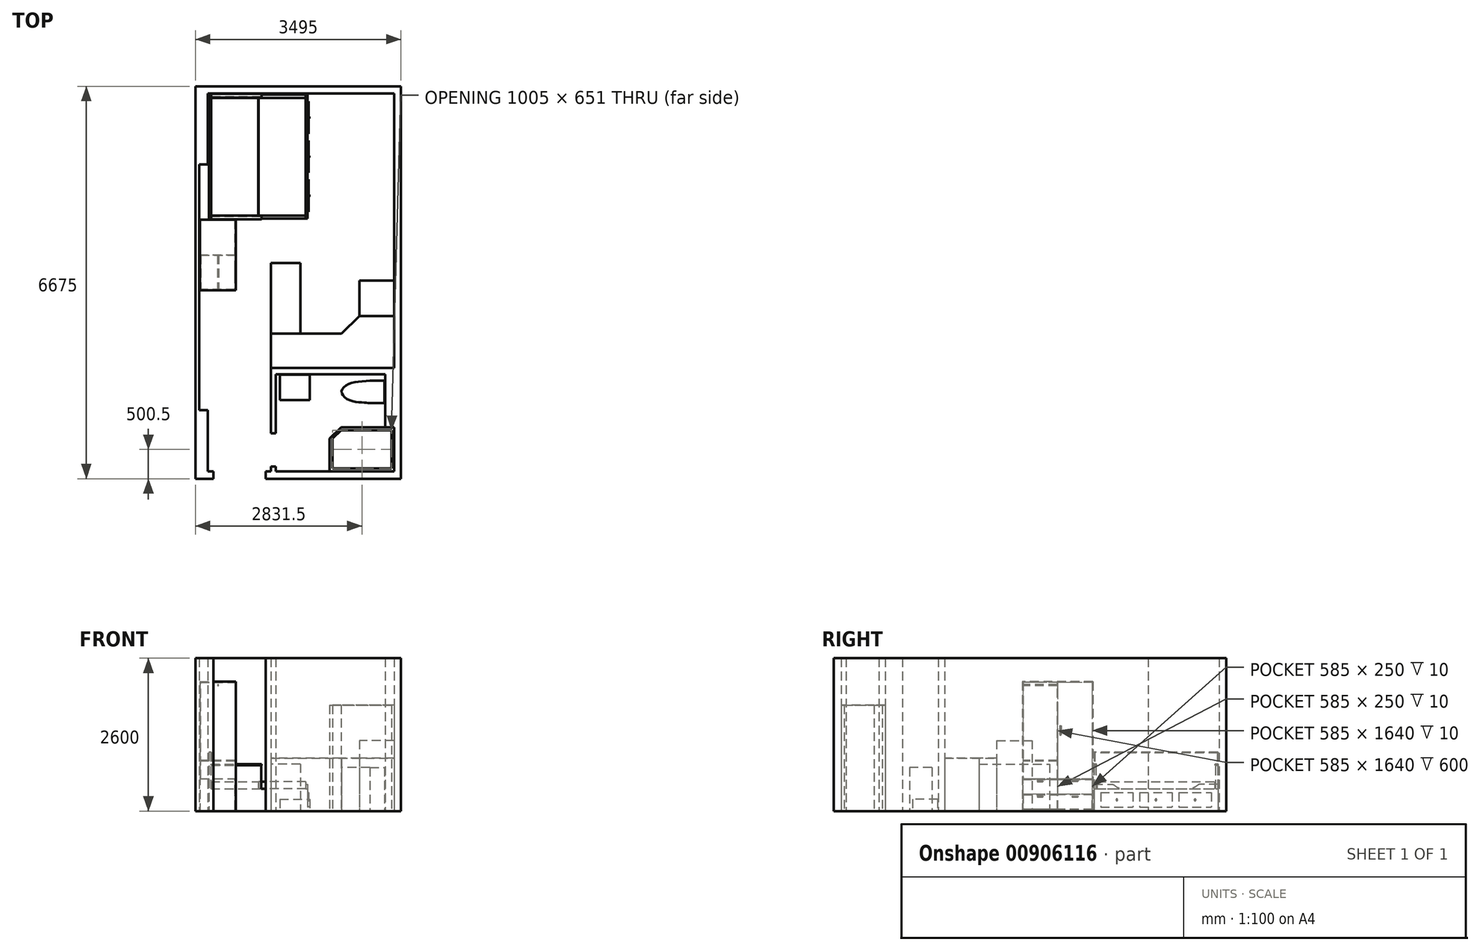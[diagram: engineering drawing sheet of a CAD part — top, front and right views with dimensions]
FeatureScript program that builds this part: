
annotation { "Feature Type Name" : "Feature", "Feature Type Description" : "" }
export const myFeature = defineFeature(function(context is Context, id is Id, definition is map)
    precondition{}
    {
        {
            var Q0;
            Q0=qCreatedBy(makeId("Top.planeOp"),FACE);
            var sketch = newSketch(context, id + "F0", { "sketchPlane" : qUnion([Q0])});
            skLineSegment(sketch, "E0", {"start": v(0, 0) * mm, "end": v(-2302, 0) * mm});
            skLineSegment(sketch, "E1", {"start": v(-3191, 0) * mm, "end": v(-3495, 0) * mm});
            skLineSegment(sketch, "E2", {"start": v(0, 0) * mm, "end": v(0, 6675) * mm});
            skLineSegment(sketch, "E3", {"start": v(0, 6675) * mm, "end": v(-3495, 6675) * mm});
            skLineSegment(sketch, "E4", {"start": v(-3495, 6675) * mm, "end": v(-3495, 0) * mm});
            skLineSegment(sketch, "E5", {"start": v(-2302, 0) * mm, "end": v(-2302, 125) * mm});
            skLineSegment(sketch, "E6", {"start": v(-2302, 125) * mm, "end": v(-2211, 125) * mm});
            skLineSegment(sketch, "E7", {"start": v(-2211, 125) * mm, "end": v(-2211, 211) * mm});
            skLineSegment(sketch, "E8", {"start": v(-2211, 211) * mm, "end": v(-2129, 211) * mm});
            skLineSegment(sketch, "E9", {"start": v(-2129, 211) * mm, "end": v(-2129, 125) * mm});
            skLineSegment(sketch, "E10", {"start": v(-2129, 125) * mm, "end": v(-116, 125) * mm});
            skLineSegment(sketch, "E11", {"start": v(-116, 125) * mm, "end": v(-116, 876) * mm});
            skLineSegment(sketch, "E12", {"start": v(-116, 876) * mm, "end": v(-269, 876) * mm});
            skLineSegment(sketch, "E13", {"start": v(-269, 876) * mm, "end": v(-269, 1780) * mm});
            skLineSegment(sketch, "E14", {"start": v(0, 1780) * mm, "end": v(-2129, 1780) * mm});
            skLineSegment(sketch, "E15", {"start": v(-2129, 1780) * mm, "end": v(-2129, 771.47) * mm});
            skLineSegment(sketch, "E16", {"start": v(-2129, 771.47) * mm, "end": v(-2211, 771.47) * mm});
            skLineSegment(sketch, "E17", {"start": v(-2211, 771.47) * mm, "end": v(-2211, 1887) * mm});
            skLineSegment(sketch, "E18", {"start": v(-2211, 1887) * mm, "end": v(0, 1887) * mm});
            skLineSegment(sketch, "E19", {"start": v(-116, 1887) * mm, "end": v(-116, 6555) * mm});
            skLineSegment(sketch, "E20", {"start": v(-116, 6555) * mm, "end": v(-3285, 6555) * mm});
            skLineSegment(sketch, "E21", {"start": v(-3285, 6555) * mm, "end": v(-3285, 5348) * mm});
            skLineSegment(sketch, "E22", {"start": v(-3285, 5348) * mm, "end": v(-3430, 5348) * mm});
            skLineSegment(sketch, "E23", {"start": v(-3430, 5348) * mm, "end": v(-3430, 1167) * mm});
            skLineSegment(sketch, "E24", {"start": v(-3495, 0) * mm, "end": v(-3191, 0) * mm});
            skLineSegment(sketch, "E25", {"start": v(-3430, 1167) * mm, "end": v(-3285, 1167) * mm});
            skLineSegment(sketch, "E26", {"start": v(-3191, 0) * mm, "end": v(-3191, 125) * mm});
            skLineSegment(sketch, "E27", {"start": v(-3191, 125) * mm, "end": v(-3285, 125) * mm});
            skLineSegment(sketch, "E28", {"start": v(-3285, 125) * mm, "end": v(-3285, 1167) * mm});
            skSolve(sketch);
        }
        {
            var Q0;
            {var subQ0=sQuery(id+"F0.wireOp",EDGE,"E0");Q0=makeQuery(id+"F0.imprint","IMPRINT",FACE,{"disambiguationData":[TD([[makeQuery(id+"F0.imprint","IMPRINT",EDGE,{"derivedFrom":subQ0}),-1.0]])]});}
            var Q1;
            {var subQ1=sQuery(id+"F0.wireOp",EDGE,"E3");Q1=makeQuery(id+"F0.imprint","IMPRINT",FACE,{"disambiguationData":[TD([[makeQuery(id+"F0.imprint","IMPRINT",EDGE,{"derivedFrom":subQ1}),1.0]])]});}
            var Q2;
            {var subQ2=sQuery(id+"F0.wireOp",EDGE,"E15");Q2=makeQuery(id+"F0.imprint","IMPRINT",FACE,{"disambiguationData":[TD([[makeQuery(id+"F0.imprint","IMPRINT",EDGE,{"derivedFrom":subQ2}),-1.0]])]});}
            extrude(context, id + "F1", {"entities" : qUnion([Q0, Q1, Q2]), "depth" : 2600 * mm, "offsetDistance" : 25 * mm});
        }
        {
            var Q0;
            Q0=makeQuery(id+"F1.opExtrude","CAP_FACE",FACE,{"disambiguationData":[OSD([sQuery(id+"F0.wireOp",EDGE,"E0"),sQuery(id+"F0.wireOp",EDGE,"E2"),sQuery(id+"F0.wireOp",EDGE,"E3"),sQuery(id+"F0.wireOp",EDGE,"E4"),sQuery(id+"F0.wireOp",EDGE,"E5"),sQuery(id+"F0.wireOp",EDGE,"E6"),sQuery(id+"F0.wireOp",EDGE,"E7"),sQuery(id+"F0.wireOp",EDGE,"E8"),sQuery(id+"F0.wireOp",EDGE,"E9"),sQuery(id+"F0.wireOp",EDGE,"E10"),sQuery(id+"F0.wireOp",EDGE,"E11"),sQuery(id+"F0.wireOp",EDGE,"E12"),sQuery(id+"F0.wireOp",EDGE,"E13"),sQuery(id+"F0.wireOp",EDGE,"E14"),sQuery(id+"F0.wireOp",EDGE,"E15"),sQuery(id+"F0.wireOp",EDGE,"E16"),sQuery(id+"F0.wireOp",EDGE,"E17"),sQuery(id+"F0.wireOp",EDGE,"E18"),sQuery(id+"F0.wireOp",EDGE,"E19"),sQuery(id+"F0.wireOp",EDGE,"E20"),sQuery(id+"F0.wireOp",EDGE,"E21"),sQuery(id+"F0.wireOp",EDGE,"E22"),sQuery(id+"F0.wireOp",EDGE,"E23"),sQuery(id+"F0.wireOp",EDGE,"E24"),sQuery(id+"F0.wireOp",EDGE,"E25"),sQuery(id+"F0.wireOp",EDGE,"E26"),sQuery(id+"F0.wireOp",EDGE,"E27"),sQuery(id+"F0.wireOp",EDGE,"E28")])],"isStart":true});
            var sketch = newSketch(context, id + "F2", { "sketchPlane" : qUnion([Q0])});
            skLineSegment(sketch, "E29", {"start": v(0, 0) * mm, "end": v(0, -2770) * mm, "construction": true});
            skLineSegment(sketch, "E30", {"start": v(-116, -1887) * mm, "end": v(-116, -2770) * mm});
            skLineSegment(sketch, "E31", {"start": v(-116, -2770) * mm, "end": v(-705, -2770) * mm});
            skLineSegment(sketch, "E32", {"start": v(-705, -2770) * mm, "end": v(-1011, -2468) * mm});
            skLineSegment(sketch, "E33", {"start": v(-1011, -2468) * mm, "end": v(-1011, -1887) * mm});
            skLineSegment(sketch, "E34", {"start": v(-1011, -1887) * mm, "end": v(-116, -1887) * mm});
            skLineSegment(sketch, "E35", {"start": v(-1011, -2468) * mm, "end": v(-2211, -2468) * mm});
            skLineSegment(sketch, "E36", {"start": v(-2211, -2468) * mm, "end": v(-2211, -1887) * mm});
            skLineSegment(sketch, "E37", {"start": v(-2211, -1887) * mm, "end": v(-1011, -1887) * mm});
            skSolve(sketch);
        }
        {
            var Q0;
            Q0=makeQuery(id+"F2.imprint","IMPRINT",FACE,{"disambiguationData":[TD([[makeQuery(id+"F2.imprint","IMPRINT",EDGE,{"derivedFrom":sQuery(id+"F2.wireOp",EDGE,"E33")}),1.0]])]});
            var Q1;
            Q1=makeQuery(id+"F2.imprint","IMPRINT",FACE,{"disambiguationData":[TD([[makeQuery(id+"F2.imprint","IMPRINT",EDGE,{"derivedFrom":sQuery(id+"F2.wireOp",EDGE,"E30")}),-1.0]])]});
            extrude(context, id + "F3", {"entities" : qUnion([Q0, Q1]), "oppositeDirection" : true, "depth" : 900 * mm, "offsetDistance" : 25 * mm});
        }
        {
            var Q0;
            Q0=makeQuery(id+"F3.opExtrude","CAP_FACE",FACE,{"disambiguationData":[OSD([sQuery(id+"F2.wireOp",EDGE,"E30"),sQuery(id+"F2.wireOp",EDGE,"E31"),sQuery(id+"F2.wireOp",EDGE,"E32"),sQuery(id+"F2.wireOp",EDGE,"E34"),sQuery(id+"F2.wireOp",EDGE,"E35"),sQuery(id+"F2.wireOp",EDGE,"E36"),sQuery(id+"F2.wireOp",EDGE,"E37")])],"isStart":true});
            var sketch = newSketch(context, id + "F4", { "sketchPlane" : qUnion([Q0])});
            skLineSegment(sketch, "E38", {"start": v(-705, -2770) * mm, "end": v(-705, -3370) * mm});
            skLineSegment(sketch, "E39", {"start": v(-705, -3370) * mm, "end": v(-116, -3370) * mm});
            skLineSegment(sketch, "E40", {"start": v(-116, -3370) * mm, "end": v(-116, -2770) * mm});
            skLineSegment(sketch, "E41", {"start": v(-116, -2770) * mm, "end": v(-705, -2770) * mm});
            skSolve(sketch);
        }
        {
            var Q0;
            Q0=makeQuery(id+"F4.imprint","IMPRINT",FACE,{"disambiguationData":[TD([[makeQuery(id+"F4.imprint","IMPRINT",EDGE,{"derivedFrom":sQuery(id+"F4.wireOp",EDGE,"E38")}),1.0]])]});
            extrude(context, id + "F5", {"entities" : qUnion([Q0]), "oppositeDirection" : true, "depth" : 1200 * mm, "offsetDistance" : 25 * mm});
        }
        {
            var Q0;
            Q0=makeQuery(id+"F5.boolean.opBoolean","MERGE",FACE,{"derivedFrom":[makeQuery(id+"F3.opExtrude","CAP_FACE",FACE,{"disambiguationData":[OSD([sQuery(id+"F2.wireOp",EDGE,"E30"),sQuery(id+"F2.wireOp",EDGE,"E31"),sQuery(id+"F2.wireOp",EDGE,"E32"),sQuery(id+"F2.wireOp",EDGE,"E34"),sQuery(id+"F2.wireOp",EDGE,"E35"),sQuery(id+"F2.wireOp",EDGE,"E36"),sQuery(id+"F2.wireOp",EDGE,"E37")])],"isStart":true}),makeQuery(id+"F5.opExtrude","CAP_FACE",FACE,{"disambiguationData":[OSD([sQuery(id+"F4.wireOp",EDGE,"E38"),sQuery(id+"F4.wireOp",EDGE,"E39"),sQuery(id+"F4.wireOp",EDGE,"E40"),sQuery(id+"F4.wireOp",EDGE,"E41")])],"isStart":true})]});
            var sketch = newSketch(context, id + "F6", { "sketchPlane" : qUnion([Q0])});
            skLineSegment(sketch, "E42", {"start": v(-3268.16, -6533.7) * mm, "end": v(-3268.16, -4423.7) * mm});
            skLineSegment(sketch, "E43", {"start": v(-3268.16, -4423.7) * mm, "end": v(-1588.16, -4423.7) * mm});
            skLineSegment(sketch, "E44", {"start": v(-1588.16, -4423.7) * mm, "end": v(-1588.16, -6533.7) * mm});
            skLineSegment(sketch, "E45", {"start": v(-1588.16, -6533.7) * mm, "end": v(-3268.16, -6533.7) * mm});
            skSolve(sketch);
        }
        {
            var Q0;
            Q0=makeQuery(id+"F6.imprint","IMPRINT",FACE,{"disambiguationData":[TD([[makeQuery(id+"F6.imprint","IMPRINT",EDGE,{"derivedFrom":sQuery(id+"F6.wireOp",EDGE,"E42")}),-1.0]])]});
            extrude(context, id + "F7", {"entities" : qUnion([Q0]), "oppositeDirection" : true, "depth" : 800 * mm, "offsetDistance" : 25 * mm});
        }
        {
            var Q0;
            Q0=makeQuery(id+"F7.opExtrude","CAP_FACE",FACE,{"disambiguationData":[OSD([sQuery(id+"F6.wireOp",EDGE,"E42"),sQuery(id+"F6.wireOp",EDGE,"E43"),sQuery(id+"F6.wireOp",EDGE,"E44"),sQuery(id+"F6.wireOp",EDGE,"E45")])],"isStart":true});
            var sketch = newSketch(context, id + "F8", { "sketchPlane" : qUnion([Q0])});
            skLineSegment(sketch, "E46.bottom", {"start": v(-3418.16, -4406.84) * mm, "end": v(-2808.16, -4406.84) * mm});
            skLineSegment(sketch, "E46.top", {"start": v(-3418.16, -3206.84) * mm, "end": v(-2808.16, -3206.84) * mm});
            skLineSegment(sketch, "E46.left", {"start": v(-3418.16, -4406.84) * mm, "end": v(-3418.16, -3206.84) * mm});
            skLineSegment(sketch, "E46.right", {"start": v(-2808.16, -4406.84) * mm, "end": v(-2808.16, -3206.84) * mm});
            skSolve(sketch);
        }
        {
            var Q0;
            Q0=makeQuery(id+"F8.imprint","IMPRINT",FACE,{"disambiguationData":[TD([[makeQuery(id+"F8.imprint","IMPRINT",EDGE,{"derivedFrom":sQuery(id+"F8.wireOp",EDGE,"E46.bottom")}),1.0]])]});
            extrude(context, id + "F9", {"entities" : qUnion([Q0]), "oppositeDirection" : true, "depth" : 2200 * mm, "offsetDistance" : 25 * mm});
        }
        {
            var Q0;
            Q0=makeQuery(id+"F3.opExtrude","CAP_FACE",FACE,{"disambiguationData":[OSD([sQuery(id+"F2.wireOp",EDGE,"E30"),sQuery(id+"F2.wireOp",EDGE,"E31"),sQuery(id+"F2.wireOp",EDGE,"E32"),sQuery(id+"F2.wireOp",EDGE,"E34"),sQuery(id+"F2.wireOp",EDGE,"E35"),sQuery(id+"F2.wireOp",EDGE,"E36"),sQuery(id+"F2.wireOp",EDGE,"E37")])],"isStart":true});
            var sketch = newSketch(context, id + "F10", { "sketchPlane" : qUnion([Q0])});
            skLineSegment(sketch, "E47", {"start": v(-2211, -2468) * mm, "end": v(-2211, -3668) * mm});
            skLineSegment(sketch, "E48", {"start": v(-2211, -3668) * mm, "end": v(-1711, -3668) * mm});
            skLineSegment(sketch, "E49", {"start": v(-1711, -3668) * mm, "end": v(-1711, -2468) * mm});
            skLineSegment(sketch, "E50", {"start": v(-1711, -2468) * mm, "end": v(-2211, -2468) * mm});
            skSolve(sketch);
        }
        {
            var Q0;
            Q0=makeQuery(id+"F10.imprint","IMPRINT",FACE,{"disambiguationData":[TD([[makeQuery(id+"F10.imprint","IMPRINT",EDGE,{"derivedFrom":sQuery(id+"F10.wireOp",EDGE,"E47")}),1.0]])]});
            extrude(context, id + "F11", {"entities" : qUnion([Q0]), "oppositeDirection" : true, "depth" : 800 * mm, "offsetDistance" : 25 * mm});
        }
        {
            var Q0;
            Q0=makeQuery(id+"F3.opExtrude","CAP_FACE",FACE,{"disambiguationData":[OSD([sQuery(id+"F2.wireOp",EDGE,"E30"),sQuery(id+"F2.wireOp",EDGE,"E31"),sQuery(id+"F2.wireOp",EDGE,"E32"),sQuery(id+"F2.wireOp",EDGE,"E34"),sQuery(id+"F2.wireOp",EDGE,"E35"),sQuery(id+"F2.wireOp",EDGE,"E36"),sQuery(id+"F2.wireOp",EDGE,"E37")])],"isStart":true});
            var sketch = newSketch(context, id + "F12", { "sketchPlane" : qUnion([Q0])});
            skLineSegment(sketch, "E51.bottom", {"start": v(-2061, -1768.17) * mm, "end": v(-1551, -1768.17) * mm});
            skLineSegment(sketch, "E51.top", {"start": v(-2061, -1338.17) * mm, "end": v(-1551, -1338.17) * mm});
            skLineSegment(sketch, "E51.left", {"start": v(-2061, -1768.17) * mm, "end": v(-2061, -1338.17) * mm});
            skLineSegment(sketch, "E51.right", {"start": v(-1551, -1768.17) * mm, "end": v(-1551, -1338.17) * mm});
            skSolve(sketch);
        }
        {
            var Q0;
            Q0 = qSketchRegion(id + "F12", true);
            extrude(context, id + "F13", {"entities" : qUnion([Q0]), "oppositeDirection" : true, "depth" : 200 * mm, "offsetDistance" : 25 * mm});
        }
        {
            var Q0;
            Q0=makeQuery(id+"F13.opExtrude","CAP_FACE",FACE,{"disambiguationData":[OSD([sQuery(id+"F12.wireOp",EDGE,"E51.bottom"),sQuery(id+"F12.wireOp",EDGE,"E51.top"),sQuery(id+"F12.wireOp",EDGE,"E51.left"),sQuery(id+"F12.wireOp",EDGE,"E51.right")])],"isStart":true});
            var sketch = newSketch(context, id + "F14", { "sketchPlane" : qUnion([Q0])});
            skLineSegment(sketch, "E52.bottom", {"start": v(-429, -1668.17) * mm, "end": v(-279, -1668.17) * mm});
            skLineSegment(sketch, "E52.top", {"start": v(-429, -1288.17) * mm, "end": v(-279, -1288.17) * mm});
            skLineSegment(sketch, "E52.left", {"start": v(-429, -1668.17) * mm, "end": v(-429, -1288.17) * mm});
            skLineSegment(sketch, "E52.right", {"start": v(-279, -1668.17) * mm, "end": v(-279, -1288.17) * mm});
            skLineSegment(sketch, "E53", {"start": v(-429, -1668.17) * mm, "end": v(-529, -1668.17) * mm});
            skLineSegment(sketch, "E54", {"start": v(-429, -1288.17) * mm, "end": v(-529, -1288.17) * mm});
            skLineSegment(sketch, "E55", {"start": v(-279, -1478.17) * mm, "end": v(-1009, -1478.17) * mm, "construction": true});
            skLineSegment(sketch, "E56", {"start": v(-807.58, -1478.17) * mm, "end": v(-807.58, -1578.17) * mm, "construction": true});
            skLineSegment(sketch, "E57", {"start": v(-807.58, -1478.17) * mm, "end": v(-807.58, -1378.17) * mm, "construction": true});
            skLineSegment(sketch, "E58", {"start": v(-644, -1478.17) * mm, "end": v(-644, -1628.17) * mm, "construction": true});
            skLineSegment(sketch, "E59", {"start": v(-644, -1478.17) * mm, "end": v(-644, -1328.17) * mm, "construction": true});
            skFitSpline(sketch, "E60", {"points": [v(-529, -1668.17) * mm, v(-896.53, -1606.51) * mm, v(-1009, -1478.17) * mm, v(-901.9, -1349.25) * mm, v(-641.95, -1295.66) * mm, v(-529, -1288.17) * mm], "startDerivative": vector(-1523.87, 89.22) * mm, "endDerivative": vector(665.63, 39.75) * mm});
            skSolve(sketch);
        }
        {
            var Q0;
            Q0=makeQuery(id+"F14.imprint","IMPRINT",FACE,{"disambiguationData":[TD([[makeQuery(id+"F14.imprint","IMPRINT",EDGE,{"derivedFrom":sQuery(id+"F14.wireOp",EDGE,"E52.bottom")}),1.0]])]});
            var Q1;
            Q1=makeQuery(id+"F14.imprint","IMPRINT",FACE,{"disambiguationData":[TD([[makeQuery(id+"F14.imprint","IMPRINT",EDGE,{"derivedFrom":sQuery(id+"F14.wireOp",EDGE,"E52.left")}),1.0]])]});
            extrude(context, id + "F15", {"entities" : qUnion([Q0, Q1]), "oppositeDirection" : true, "depth" : 740 * mm, "offsetDistance" : 25 * mm});
        }
        {
            var Q0;
            Q0=makeQuery(id+"F1.opExtrude","CAP_FACE",FACE,{"disambiguationData":[OSD([sQuery(id+"F0.wireOp",EDGE,"E0"),sQuery(id+"F0.wireOp",EDGE,"E2"),sQuery(id+"F0.wireOp",EDGE,"E3"),sQuery(id+"F0.wireOp",EDGE,"E4"),sQuery(id+"F0.wireOp",EDGE,"E5"),sQuery(id+"F0.wireOp",EDGE,"E6"),sQuery(id+"F0.wireOp",EDGE,"E7"),sQuery(id+"F0.wireOp",EDGE,"E8"),sQuery(id+"F0.wireOp",EDGE,"E9"),sQuery(id+"F0.wireOp",EDGE,"E10"),sQuery(id+"F0.wireOp",EDGE,"E11"),sQuery(id+"F0.wireOp",EDGE,"E12"),sQuery(id+"F0.wireOp",EDGE,"E13"),sQuery(id+"F0.wireOp",EDGE,"E14"),sQuery(id+"F0.wireOp",EDGE,"E15"),sQuery(id+"F0.wireOp",EDGE,"E16"),sQuery(id+"F0.wireOp",EDGE,"E17"),sQuery(id+"F0.wireOp",EDGE,"E18"),sQuery(id+"F0.wireOp",EDGE,"E19"),sQuery(id+"F0.wireOp",EDGE,"E20"),sQuery(id+"F0.wireOp",EDGE,"E21"),sQuery(id+"F0.wireOp",EDGE,"E22"),sQuery(id+"F0.wireOp",EDGE,"E23"),sQuery(id+"F0.wireOp",EDGE,"E24"),sQuery(id+"F0.wireOp",EDGE,"E25"),sQuery(id+"F0.wireOp",EDGE,"E26"),sQuery(id+"F0.wireOp",EDGE,"E27"),sQuery(id+"F0.wireOp",EDGE,"E28")])],"isStart":true});
            var sketch = newSketch(context, id + "F16", { "sketchPlane" : qUnion([Q0])});
            skLineSegment(sketch, "E61", {"start": v(-116, -876) * mm, "end": v(-1016, -876) * mm});
            skLineSegment(sketch, "E62", {"start": v(-1016, -876) * mm, "end": v(-1216, -684.67) * mm});
            skLineSegment(sketch, "E63", {"start": v(-1216, -684.67) * mm, "end": v(-1216, -125) * mm});
            skLineSegment(sketch, "E64", {"start": v(-1216, -125) * mm, "end": v(-116, -125) * mm});
            skLineSegment(sketch, "E65", {"start": v(-116, -125) * mm, "end": v(-116, -876) * mm});
            skLineSegment(sketch, "E66.0", {"start": v(-1166, -684.67) * mm, "end": v(-1166, -175) * mm});
            skLineSegment(sketch, "E67.0", {"start": v(-1166, -175) * mm, "end": v(-161, -175) * mm});
            skLineSegment(sketch, "E68.0", {"start": v(-161, -826) * mm, "end": v(-1016, -826) * mm});
            skLineSegment(sketch, "E69.0", {"start": v(-111, -125) * mm, "end": v(-111, -876) * mm});
            skLineSegment(sketch, "E70.0", {"start": v(-112.7, -125) * mm, "end": v(-112.7, -876) * mm});
            skLineSegment(sketch, "E71.0", {"start": v(-161, -175) * mm, "end": v(-161, -826) * mm});
            skLineSegment(sketch, "E72", {"start": v(-1166, -684.67) * mm, "end": v(-1016, -826) * mm});
            skSolve(sketch);
        }
        {
            var Q0;
            {var subQ3=sQuery(id+"F16.wireOp",EDGE,"E62");Q0=makeQuery(id+"F16.imprint","IMPRINT",FACE,{"disambiguationData":[TD([[makeQuery(id+"F16.imprint","IMPRINT",EDGE,{"derivedFrom":subQ3}),-1.0]])]});}
            extrude(context, id + "F17", {"entities" : qUnion([Q0]), "oppositeDirection" : true, "depth" : 1800 * mm, "offsetDistance" : 25 * mm});
        }
        {
            var Q0;
            Q0=makeQuery(id+"F9.opExtrude","SWEPT_FACE",FACE,{"disambiguationData":[OSD([sQuery(id+"F8.wireOp",EDGE,"E46.right")])]});
            var sketch = newSketch(context, id + "F18", { "sketchPlane" : qUnion([Q0])});
            skLineSegment(sketch, "E73", {"start": v(3206.84, 2200) * mm, "end": v(3206.84, 0) * mm, "construction": true});
            skLineSegment(sketch, "E74", {"start": v(3206.84, 0) * mm, "end": v(3206.84, 2200) * mm});
            skLineSegment(sketch, "E75", {"start": v(4406.84, 2200) * mm, "end": v(4406.84, 0) * mm});
            skLineSegment(sketch, "E76", {"start": v(4406.84, 0) * mm, "end": v(3206.84, 0) * mm});
            skLineSegment(sketch, "E77.0", {"start": v(4396.84, 30) * mm, "end": v(3216.84, 30) * mm});
            skLineSegment(sketch, "E78.0", {"start": v(3216.84, 30) * mm, "end": v(3216.84, 0) * mm});
            skLineSegment(sketch, "E79.0", {"start": v(4396.84, 30) * mm, "end": v(4396.84, 0) * mm});
            skSolve(sketch);
        }
        {
            var Q0;
            Q0 = qSketchRegion(id + "F18", true);
            extrude(context, id + "F19", {"entities" : qUnion([Q0]), "operationType" : NewBodyOperationType.REMOVE, "oppositeDirection" : true, "depth" : 20 * mm, "offsetDistance" : 25 * mm});
        }
        {
            var Q0;
            Q0=makeQuery(id+"F9.opExtrude","SWEPT_FACE",FACE,{"disambiguationData":[OSD([sQuery(id+"F8.wireOp",EDGE,"E46.right")])]});
            var sketch = newSketch(context, id + "F20", { "sketchPlane" : qUnion([Q0])});
            skLineSegment(sketch, "E80.bottom", {"start": v(4406.84, 0) * mm, "end": v(3206.84, 0) * mm});
            skLineSegment(sketch, "E80.top", {"start": v(4406.84, 2200) * mm, "end": v(3206.84, 2200) * mm});
            skLineSegment(sketch, "E80.left", {"start": v(4406.84, 0) * mm, "end": v(4406.84, 2200) * mm});
            skLineSegment(sketch, "E80.right", {"start": v(3206.84, 0) * mm, "end": v(3206.84, 2200) * mm});
            skLineSegment(sketch, "E81", {"start": v(3206.84, 0) * mm, "end": v(3206.84, 550) * mm, "construction": true});
            skLineSegment(sketch, "E82", {"start": v(3216.84, 30) * mm, "end": v(3216.84, 280) * mm});
            skLineSegment(sketch, "E83", {"start": v(3216.84, 280) * mm, "end": v(3216.84, 290) * mm});
            skLineSegment(sketch, "E84", {"start": v(3806.84, 30) * mm, "end": v(3806.84, 639.76) * mm, "construction": true});
            skLineSegment(sketch, "E85.0", {"start": v(3801.84, 30) * mm, "end": v(3801.84, 290) * mm});
            skLineSegment(sketch, "E86", {"start": v(3216.84, 280) * mm, "end": v(3801.84, 280) * mm});
            skLineSegment(sketch, "E87", {"start": v(3801.84, 30) * mm, "end": v(3216.84, 30) * mm});
            skLineSegment(sketch, "E88.MirrorCS", {"start": v(4396.84, 280) * mm, "end": v(4396.84, 290) * mm});
            skLineSegment(sketch, "E89.MirrorCS", {"start": v(3811.84, 30) * mm, "end": v(4396.84, 30) * mm});
            skLineSegment(sketch, "E90.MirrorCS", {"start": v(4396.84, 30) * mm, "end": v(4396.84, 280) * mm});
            skLineSegment(sketch, "E91.MirrorCS", {"start": v(4396.84, 280) * mm, "end": v(3811.84, 280) * mm});
            skLineSegment(sketch, "E92.MirrorCS", {"start": v(3811.84, 30) * mm, "end": v(3811.84, 290) * mm});
            skSolve(sketch);
        }
        {
            var Q0;
            Q0=makeQuery(id+"F20.imprint","IMPRINT",FACE,{"disambiguationData":[TD([[makeQuery(id+"F20.imprint","IMPRINT",EDGE,{"derivedFrom":sQuery(id+"F20.wireOp",EDGE,"E82")}),-1.0]])]});
            var Q1;
            {var subQ0=sQuery(id+"F20.wireOp",EDGE,"E89.MirrorCS");Q1=makeQuery(id+"F20.imprint","IMPRINT",FACE,{"disambiguationData":[TD([[makeQuery(id+"F20.imprint","IMPRINT",EDGE,{"derivedFrom":subQ0}),-1.0]])]});}
            extrude(context, id + "F21", {"entities" : qUnion([Q0, Q1]), "operationType" : NewBodyOperationType.REMOVE, "oppositeDirection" : true, "depth" : 10 * mm, "offsetDistance" : 25 * mm});
        }
        {
            var Q0;
            Q0=makeQuery(id+"F9.opExtrude","SWEPT_FACE",FACE,{"disambiguationData":[OSD([sQuery(id+"F8.wireOp",EDGE,"E46.right")])]});
            var sketch = newSketch(context, id + "F22", { "sketchPlane" : qUnion([Q0])});
            skLineSegment(sketch, "E93", {"start": v(3216.84, 280) * mm, "end": v(4396.84, 280) * mm, "construction": true});
            skLineSegment(sketch, "E94.0", {"start": v(3216.84, 290) * mm, "end": v(4396.84, 290) * mm});
            skLineSegment(sketch, "E95", {"start": v(3216.84, 290) * mm, "end": v(3216.84, 540) * mm});
            skLineSegment(sketch, "E96", {"start": v(3216.84, 540) * mm, "end": v(3801.84, 540) * mm});
            skLineSegment(sketch, "E97", {"start": v(3801.84, 540) * mm, "end": v(3801.84, 290) * mm});
            skLineSegment(sketch, "E98", {"start": v(3801.84, 290) * mm, "end": v(3216.84, 290) * mm});
            skLineSegment(sketch, "E99", {"start": v(3811.84, 290) * mm, "end": v(3811.84, 540) * mm});
            skLineSegment(sketch, "E100", {"start": v(3811.84, 540) * mm, "end": v(4396.84, 540) * mm});
            skLineSegment(sketch, "E101", {"start": v(4396.84, 540) * mm, "end": v(4396.84, 290) * mm});
            skSolve(sketch);
        }
        {
            var Q0;
            {var subQ0=sQuery(id+"F22.wireOp",EDGE,"E95");Q0=makeQuery(id+"F22.imprint","IMPRINT",FACE,{"disambiguationData":[TD([[makeQuery(id+"F22.imprint","IMPRINT",EDGE,{"derivedFrom":subQ0}),-1.0]])]});}
            var Q1;
            {var subQ0=sQuery(id+"F22.wireOp",EDGE,"E99");Q1=makeQuery(id+"F22.imprint","IMPRINT",FACE,{"disambiguationData":[TD([[makeQuery(id+"F22.imprint","IMPRINT",EDGE,{"derivedFrom":subQ0}),-1.0]])]});}
            extrude(context, id + "F23", {"entities" : qUnion([Q0, Q1]), "operationType" : NewBodyOperationType.REMOVE, "oppositeDirection" : true, "depth" : 10 * mm, "offsetDistance" : 25 * mm});
        }
        {
            var Q0;
            Q0=makeQuery(id+"F23.boolean.opBoolean","COPY",FACE,{"derivedFrom":makeQuery(id+"F23.opExtrude","CAP_FACE",FACE,{"disambiguationData":[OSD([sQuery(id+"F22.wireOp",EDGE,"E94.0"),sQuery(id+"F22.wireOp",EDGE,"E99"),sQuery(id+"F22.wireOp",EDGE,"E100"),sQuery(id+"F22.wireOp",EDGE,"E101")])],"isStart":false})});
            var sketch = newSketch(context, id + "F24", { "sketchPlane" : qUnion([Q0])});
            skLineSegment(sketch, "E102", {"start": v(3509.34, 540) * mm, "end": v(3509.34, 0) * mm, "construction": true});
            skLineSegment(sketch, "E103.bottom", {"start": v(3459.34, 510) * mm, "end": v(3559.34, 510) * mm});
            skLineSegment(sketch, "E103.top", {"start": v(3459.34, 501) * mm, "end": v(3559.34, 501) * mm});
            skLineSegment(sketch, "E103.left", {"start": v(3459.34, 510) * mm, "end": v(3459.34, 501) * mm});
            skLineSegment(sketch, "E103.right", {"start": v(3559.34, 510) * mm, "end": v(3559.34, 501) * mm});
            skLineSegment(sketch, "E104.bottom", {"start": v(3459.34, 250) * mm, "end": v(3559.34, 250) * mm});
            skLineSegment(sketch, "E104.top", {"start": v(3459.34, 241) * mm, "end": v(3559.34, 241) * mm});
            skLineSegment(sketch, "E104.left", {"start": v(3459.34, 250) * mm, "end": v(3459.34, 241) * mm});
            skLineSegment(sketch, "E104.right", {"start": v(3559.34, 250) * mm, "end": v(3559.34, 241) * mm});
            skLineSegment(sketch, "E105", {"start": v(3559.34, 501) * mm, "end": v(4369.07, 510) * mm, "construction": true});
            skLineSegment(sketch, "E106", {"start": v(3559.34, 241) * mm, "end": v(4369.07, 241) * mm, "construction": true});
            skLineSegment(sketch, "E107.bottom", {"start": v(4054.34, 515.5) * mm, "end": v(4154.34, 515.5) * mm});
            skLineSegment(sketch, "E107.top", {"start": v(4054.34, 506.5) * mm, "end": v(4154.34, 506.5) * mm});
            skLineSegment(sketch, "E107.left", {"start": v(4054.34, 515.5) * mm, "end": v(4054.34, 506.5) * mm});
            skLineSegment(sketch, "E107.right", {"start": v(4154.34, 515.5) * mm, "end": v(4154.34, 506.5) * mm});
            skLineSegment(sketch, "E108", {"start": v(4104.34, 540) * mm, "end": v(4110.74, -35.36) * mm, "construction": true});
            skLineSegment(sketch, "E109.bottom", {"start": v(4054.34, 250) * mm, "end": v(4154.34, 250) * mm});
            skLineSegment(sketch, "E109.top", {"start": v(4054.34, 241) * mm, "end": v(4154.34, 241) * mm});
            skLineSegment(sketch, "E109.left", {"start": v(4054.34, 250) * mm, "end": v(4054.34, 241) * mm});
            skLineSegment(sketch, "E109.right", {"start": v(4154.34, 250) * mm, "end": v(4154.34, 241) * mm});
            skSolve(sketch);
        }
        {
            var Q0;
            Q0=makeQuery(id+"F24.imprint","IMPRINT",FACE,{"disambiguationData":[TD([[makeQuery(id+"F24.imprint","IMPRINT",EDGE,{"derivedFrom":sQuery(id+"F24.wireOp",EDGE,"E107.bottom")}),-1.0]])]});
            var Q1;
            Q1=makeQuery(id+"F24.imprint","IMPRINT",FACE,{"disambiguationData":[TD([[makeQuery(id+"F24.imprint","IMPRINT",EDGE,{"derivedFrom":sQuery(id+"F24.wireOp",EDGE,"E109.bottom")}),-1.0]])]});
            var Q2;
            Q2=makeQuery(id+"F24.imprint","IMPRINT",FACE,{"disambiguationData":[TD([[makeQuery(id+"F24.imprint","IMPRINT",EDGE,{"derivedFrom":sQuery(id+"F24.wireOp",EDGE,"E104.bottom")}),-1.0]])]});
            var Q3;
            Q3=makeQuery(id+"F24.imprint","IMPRINT",FACE,{"disambiguationData":[TD([[makeQuery(id+"F24.imprint","IMPRINT",EDGE,{"derivedFrom":sQuery(id+"F24.wireOp",EDGE,"E103.bottom")}),-1.0]])]});
            extrude(context, id + "F25", {"entities" : qUnion([Q0, Q1, Q2, Q3]), "depth" : 10 * mm, "offsetDistance" : 25 * mm});
        }
        {
            var Q0;
            Q0=makeQuery(id+"F9.opExtrude","SWEPT_FACE",FACE,{"disambiguationData":[OSD([sQuery(id+"F8.wireOp",EDGE,"E46.right")])]});
            var sketch = newSketch(context, id + "F26", { "sketchPlane" : qUnion([Q0])});
            skLineSegment(sketch, "E110.0", {"start": v(4406.84, 2190) * mm, "end": v(3206.84, 2190) * mm});
            skLineSegment(sketch, "E111.0", {"start": v(3216.84, 2200) * mm, "end": v(3216.84, 0) * mm});
            skLineSegment(sketch, "E112", {"start": v(3206.84, 540) * mm, "end": v(4406.84, 540) * mm, "construction": true});
            skLineSegment(sketch, "E113.0", {"start": v(4396.84, 2200) * mm, "end": v(4396.84, 0) * mm});
            skLineSegment(sketch, "E114.0", {"start": v(3206.84, 550) * mm, "end": v(4406.84, 550) * mm});
            skLineSegment(sketch, "E115", {"start": v(3801.84, 540) * mm, "end": v(3801.84, 2190) * mm});
            skLineSegment(sketch, "E116", {"start": v(3811.84, 540) * mm, "end": v(3811.84, 2190) * mm});
            skSolve(sketch);
        }
        {
            var Q0;
            {var subQ0=sQuery(id+"F26.wireOp",EDGE,"E115");var subQ1=sQuery(id+"F26.wireOp",EDGE,"E110.0");var subQ2=makeQuery(id+"F26.imprint","INTERSECT",VERTEX,{"derivedFrom":[subQ1,subQ0]});Q0=makeQuery(id+"F26.imprint","IMPRINT",FACE,{"disambiguationData":[TD([[makeQuery(id+"F26.imprint","IMPRINT",EDGE,{"disambiguationData":[TD([[subQ2,-1.0]])],"derivedFrom":subQ1}),1.0]])]});}
            var Q1;
            {var subQ0=sQuery(id+"F26.wireOp",EDGE,"E116");var subQ1=sQuery(id+"F26.wireOp",EDGE,"E110.0");var subQ2=makeQuery(id+"F26.imprint","INTERSECT",VERTEX,{"derivedFrom":[subQ1,subQ0]});Q1=makeQuery(id+"F26.imprint","IMPRINT",FACE,{"disambiguationData":[TD([[makeQuery(id+"F26.imprint","IMPRINT",EDGE,{"disambiguationData":[TD([[subQ2,1.0]])],"derivedFrom":subQ1}),1.0]])]});}
            extrude(context, id + "F27", {"entities" : qUnion([Q0, Q1]), "operationType" : NewBodyOperationType.REMOVE, "oppositeDirection" : true, "depth" : 10 * mm, "offsetDistance" : 25 * mm});
        }
        {
            var Q0;
            Q0=makeQuery(id+"F27.boolean.opBoolean","COPY",FACE,{"derivedFrom":makeQuery(id+"F27.opExtrude","CAP_FACE",FACE,{"disambiguationData":[OSD([sQuery(id+"F26.wireOp",EDGE,"E110.0"),sQuery(id+"F26.wireOp",EDGE,"E111.0"),sQuery(id+"F26.wireOp",EDGE,"E114.0"),sQuery(id+"F26.wireOp",EDGE,"E115")])],"isStart":false})});
            var sketch = newSketch(context, id + "F28", { "sketchPlane" : qUnion([Q0])});
            skLineSegment(sketch, "E117.bottom", {"start": v(3216.84, 2190) * mm, "end": v(3801.84, 2190) * mm});
            skLineSegment(sketch, "E117.top", {"start": v(3216.84, 550) * mm, "end": v(3801.84, 550) * mm});
            skLineSegment(sketch, "E117.left", {"start": v(3216.84, 2190) * mm, "end": v(3216.84, 550) * mm});
            skLineSegment(sketch, "E117.right", {"start": v(3801.84, 2190) * mm, "end": v(3801.84, 550) * mm});
            skSolve(sketch);
        }
        {
            var Q0;
            Q0 = qSketchRegion(id + "F28", true);
            extrude(context, id + "F29", {"entities" : qUnion([Q0]), "operationType" : NewBodyOperationType.REMOVE, "oppositeDirection" : true, "depth" : 590 * mm, "offsetDistance" : 25 * mm});
        }
        {
            var Q0;
            Q0=makeQuery(id+"F27.boolean.opBoolean","COPY",FACE,{"derivedFrom":makeQuery(id+"F27.opExtrude","CAP_FACE",FACE,{"disambiguationData":[OSD([sQuery(id+"F26.wireOp",EDGE,"E110.0"),sQuery(id+"F26.wireOp",EDGE,"E113.0"),sQuery(id+"F26.wireOp",EDGE,"E114.0"),sQuery(id+"F26.wireOp",EDGE,"E116")])],"isStart":false})});
            var sketch = newSketch(context, id + "F30", { "sketchPlane" : qUnion([Q0])});
            skLineSegment(sketch, "E118", {"start": v(3811.84, 1370) * mm, "end": v(4396.84, 1370) * mm, "construction": true});
            skLineSegment(sketch, "E119.bottom", {"start": v(3841.84, 1450) * mm, "end": v(3866.84, 1450) * mm});
            skLineSegment(sketch, "E119.top", {"start": v(3841.84, 1290) * mm, "end": v(3866.84, 1290) * mm});
            skLineSegment(sketch, "E119.left", {"start": v(3841.84, 1450) * mm, "end": v(3841.84, 1290) * mm});
            skLineSegment(sketch, "E119.right", {"start": v(3866.84, 1450) * mm, "end": v(3866.84, 1290) * mm});
            skSolve(sketch);
        }
        {
            var Q0;
            Q0=makeQuery(id+"F30.imprint","IMPRINT",FACE,{"disambiguationData":[TD([[makeQuery(id+"F30.imprint","IMPRINT",EDGE,{"derivedFrom":sQuery(id+"F30.wireOp",EDGE,"E119.bottom")}),-1.0]])]});
            extrude(context, id + "F31", {"entities" : qUnion([Q0]), "depth" : 10 * mm, "offsetDistance" : 25 * mm});
        }
        {
            var Q0;
            Q0=makeQuery(id+"F29.boolean.opBoolean","MERGE",FACE,{"derivedFrom":[makeQuery(id+"F27.boolean.opBoolean","COPY",FACE,{"derivedFrom":makeQuery(id+"F27.opExtrude","SWEPT_FACE",FACE,{"disambiguationData":[OSD([sQuery(id+"F26.wireOp",EDGE,"E111.0")])]})})],"fromTools":[makeQuery(id+"F29.opExtrude","SWEPT_FACE",FACE,{"disambiguationData":[OSD([sQuery(id+"F28.wireOp",EDGE,"E117.left")])]})]});
            var sketch = newSketch(context, id + "F32", { "sketchPlane" : qUnion([Q0])});
            skLineSegment(sketch, "E120", {"start": v(2808.16, 2190) * mm, "end": v(2808.16, 2140) * mm, "construction": true});
            skLineSegment(sketch, "E121", {"start": v(2808.16, 2140) * mm, "end": v(3412.96, 2140) * mm, "construction": true});
            skCircle(sketch, "E122", {"center": v(3110.56, 2140) * mm, "radius": 7.5 * mm});
            skSolve(sketch);
        }
        {
            var Q0;
            Q0 = qSketchRegion(id + "F32", true);
            extrude(context, id + "F33", {"entities" : qUnion([Q0]), "depth" : 585 * mm, "offsetDistance" : 25 * mm});
        }
        {
            var Q0;
            Q0=makeQuery(id+"F29.boolean.opBoolean","MERGE",FACE,{"derivedFrom":[makeQuery(id+"F27.boolean.opBoolean","COPY",FACE,{"derivedFrom":makeQuery(id+"F27.opExtrude","SWEPT_FACE",FACE,{"disambiguationData":[OSD([sQuery(id+"F26.wireOp",EDGE,"E111.0")])]})})],"fromTools":[makeQuery(id+"F29.opExtrude","SWEPT_FACE",FACE,{"disambiguationData":[OSD([sQuery(id+"F28.wireOp",EDGE,"E117.left")])]})]});
            var sketch = newSketch(context, id + "F34", { "sketchPlane" : qUnion([Q0])});
            skLineSegment(sketch, "E123", {"start": v(2808.16, 550) * mm, "end": v(2808.16, 850) * mm, "construction": true});
            skLineSegment(sketch, "E124", {"start": v(2808.16, 850) * mm, "end": v(2823.16, 850) * mm, "construction": true});
            skLineSegment(sketch, "E125", {"start": v(2823.16, 850) * mm, "end": v(3408.16, 850) * mm});
            skLineSegment(sketch, "E126.0", {"start": v(2823.16, 860) * mm, "end": v(3408.16, 860) * mm});
            skLineSegment(sketch, "E127", {"start": v(2823.16, 860) * mm, "end": v(2823.16, 850) * mm});
            skLineSegment(sketch, "E128", {"start": v(3408.16, 860) * mm, "end": v(3408.16, 850) * mm});
            skSolve(sketch);
        }
        {
            var Q0;
            Q0=makeQuery(id+"F34.imprint","IMPRINT",FACE,{"disambiguationData":[TD([[makeQuery(id+"F34.imprint","IMPRINT",EDGE,{"derivedFrom":sQuery(id+"F34.wireOp",EDGE,"E125")}),1.0]])]});
            extrude(context, id + "F35", {"entities" : qUnion([Q0]), "depth" : 585 * mm, "offsetDistance" : 25 * mm});
        }
        {
            var Q0;
            Q0=makeQuery(id+"F7.opExtrude","CAP_FACE",FACE,{"disambiguationData":[OSD([sQuery(id+"F6.wireOp",EDGE,"E42"),sQuery(id+"F6.wireOp",EDGE,"E43"),sQuery(id+"F6.wireOp",EDGE,"E44"),sQuery(id+"F6.wireOp",EDGE,"E45")])],"isStart":false});
            var sketch = newSketch(context, id + "F36", { "sketchPlane" : qUnion([Q0])});
            skLineSegment(sketch, "E129.bottom", {"start": v(-3268.16, 4423.7) * mm, "end": v(-1588.16, 4423.7) * mm});
            skLineSegment(sketch, "E129.top", {"start": v(-3268.16, 6533.7) * mm, "end": v(-1588.16, 6533.7) * mm});
            skLineSegment(sketch, "E129.left", {"start": v(-3268.16, 4423.7) * mm, "end": v(-3268.16, 6533.7) * mm});
            skLineSegment(sketch, "E129.right", {"start": v(-1588.16, 4423.7) * mm, "end": v(-1588.16, 6533.7) * mm});
            skLineSegment(sketch, "E130.0", {"start": v(-3268.16, 4463.7) * mm, "end": v(-1588.16, 4463.7) * mm});
            skLineSegment(sketch, "E131", {"start": v(-1588.16, 5478.7) * mm, "end": v(-3268.16, 5478.7) * mm, "construction": true});
            skLineSegment(sketch, "E132.MirrorCS", {"start": v(-3268.16, 6493.7) * mm, "end": v(-1588.16, 6493.7) * mm});
            skLineSegment(sketch, "E133.0", {"start": v(-3228.16, 4423.7) * mm, "end": v(-3228.16, 6533.7) * mm});
            skLineSegment(sketch, "E134", {"start": v(-3268.16, 4463.7) * mm, "end": v(-2378.16, 4463.7) * mm, "construction": true});
            skLineSegment(sketch, "E135", {"start": v(-2378.16, 4463.7) * mm, "end": v(-2378.16, 6493.7) * mm});
            skSolve(sketch);
        }
        {
            var Q0;
            {var subQ0=sQuery(id+"F36.wireOp",EDGE,"E135");Q0=makeQuery(id+"F36.imprint","IMPRINT",FACE,{"disambiguationData":[TD([[makeQuery(id+"F36.imprint","IMPRINT",EDGE,{"derivedFrom":subQ0}),1.0]])]});}
            extrude(context, id + "F37", {"entities" : qUnion([Q0]), "operationType" : NewBodyOperationType.REMOVE, "oppositeDirection" : true, "depth" : 420 * mm, "offsetDistance" : 25 * mm});
        }
        {
            var Q0;
            Q0=makeQuery(id+"F7.opExtrude","CAP_FACE",FACE,{"disambiguationData":[OSD([sQuery(id+"F6.wireOp",EDGE,"E42"),sQuery(id+"F6.wireOp",EDGE,"E43"),sQuery(id+"F6.wireOp",EDGE,"E44"),sQuery(id+"F6.wireOp",EDGE,"E45")])],"isStart":false});
            var sketch = newSketch(context, id + "F38", { "sketchPlane" : qUnion([Q0])});
            skLineSegment(sketch, "E136.bottom", {"start": v(-1588.16, 4423.7) * mm, "end": v(-2378.16, 4423.7) * mm});
            skLineSegment(sketch, "E136.top", {"start": v(-1588.16, 6533.7) * mm, "end": v(-2378.16, 6533.7) * mm});
            skLineSegment(sketch, "E136.left", {"start": v(-1588.16, 4423.7) * mm, "end": v(-1588.16, 6533.7) * mm});
            skLineSegment(sketch, "E136.right", {"start": v(-2378.16, 4423.7) * mm, "end": v(-2378.16, 6533.7) * mm});
            skSolve(sketch);
        }
        {
            var Q0;
            {var subQ2=sQuery(id+"F38.wireOp",EDGE,"E136.bottom");Q0=makeQuery(id+"F38.imprint","IMPRINT",FACE,{"disambiguationData":[TD([[makeQuery(id+"F38.imprint","IMPRINT",EDGE,{"derivedFrom":subQ2}),1.0]])]});}
            extrude(context, id + "F39", {"entities" : qUnion([Q0]), "operationType" : NewBodyOperationType.REMOVE, "oppositeDirection" : true, "depth" : 420 * mm, "offsetDistance" : 25 * mm});
        }
        {
            var Q0;
            Q0=makeQuery(id+"F7.opExtrude","SWEPT_FACE",FACE,{"disambiguationData":[OSD([sQuery(id+"F6.wireOp",EDGE,"E44")])]});
            var sketch = newSketch(context, id + "F40", { "sketchPlane" : qUnion([Q0])});
            skLineSegment(sketch, "E137.bottom", {"start": v(4423.7, 380) * mm, "end": v(6533.7, 380) * mm});
            skLineSegment(sketch, "E137.top", {"start": v(4423.7, 0) * mm, "end": v(6533.7, 0) * mm});
            skLineSegment(sketch, "E137.left", {"start": v(4423.7, 380) * mm, "end": v(4423.7, 0) * mm});
            skLineSegment(sketch, "E137.right", {"start": v(6533.7, 380) * mm, "end": v(6533.7, 0) * mm});
            skLineSegment(sketch, "E138", {"start": v(4423.7, 380) * mm, "end": v(4723.7, 380) * mm, "construction": true});
            skLineSegment(sketch, "E139", {"start": v(6533.7, 380) * mm, "end": v(6233.7, 380) * mm, "construction": true});
            skLineSegment(sketch, "E140", {"start": v(4723.7, 455) * mm, "end": v(4723.7, 380) * mm, "construction": true});
            skLineSegment(sketch, "E141", {"start": v(6233.7, 455) * mm, "end": v(6233.7, 380) * mm, "construction": true});
            skLineSegment(sketch, "E142", {"start": v(4423.7, 455) * mm, "end": v(4723.7, 455) * mm});
            skFitSpline(sketch, "E143", {"points": [v(4723.7, 455) * mm, v(4755.3, 448.84) * mm, v(4841.34, 393.86) * mm, v(4897.9, 380) * mm], "startDerivative": vector(115.26, -0.49) * mm, "endDerivative": vector(162.18, -14.72) * mm});
            skLineSegment(sketch, "E144", {"start": v(5478.7, 0) * mm, "end": v(5478.7, 380) * mm, "construction": true});
            skFitSpline(sketch, "E145.MirrorCS", {"points": [v(6233.7, 455) * mm, v(6202.1, 448.84) * mm, v(6116.06, 393.86) * mm, v(6059.5, 380) * mm], "startDerivative": vector(-115.26, -0.49) * mm, "endDerivative": vector(-162.18, -14.72) * mm});
            skLineSegment(sketch, "E146.MirrorCS", {"start": v(6533.7, 455) * mm, "end": v(6233.7, 455) * mm});
            skLineSegment(sketch, "E147.bottom", {"start": v(6233.7, 455) * mm, "end": v(6533.7, 455) * mm});
            skLineSegment(sketch, "E147.top", {"start": v(6233.7, 380) * mm, "end": v(6533.7, 380) * mm});
            skLineSegment(sketch, "E147.left", {"start": v(6233.7, 455) * mm, "end": v(6233.7, 380) * mm});
            skLineSegment(sketch, "E147.right", {"start": v(6533.7, 455) * mm, "end": v(6533.7, 380) * mm});
            skLineSegment(sketch, "E148.top", {"start": v(4423.7, 380) * mm, "end": v(4723.7, 380) * mm});
            skLineSegment(sketch, "E148.left", {"start": v(4423.7, 455) * mm, "end": v(4423.7, 380) * mm});
            skLineSegment(sketch, "E148.right", {"start": v(4723.7, 455) * mm, "end": v(4723.7, 380) * mm});
            skSolve(sketch);
        }
        {
            var Q0;
            Q0=makeQuery(id+"F40.imprint","IMPRINT",FACE,{"disambiguationData":[TD([[makeQuery(id+"F40.imprint","IMPRINT",EDGE,{"derivedFrom":sQuery(id+"F40.wireOp",EDGE,"E142")}),-1.0]])]});
            var Q1;
            {var subQ0=sQuery(id+"F40.wireOp",EDGE,"E143");Q1=makeQuery(id+"F40.imprint","IMPRINT",FACE,{"disambiguationData":[TD([[makeQuery(id+"F40.imprint","IMPRINT",EDGE,{"derivedFrom":subQ0}),-1.0]])]});}
            var Q2;
            {var subQ0=sQuery(id+"F40.wireOp",EDGE,"E145.MirrorCS");Q2=makeQuery(id+"F40.imprint","IMPRINT",FACE,{"disambiguationData":[TD([[makeQuery(id+"F40.imprint","IMPRINT",EDGE,{"derivedFrom":subQ0}),1.0]])]});}
            var Q3;
            Q3=makeQuery(id+"F40.imprint","IMPRINT",FACE,{"disambiguationData":[TD([[makeQuery(id+"F40.imprint","IMPRINT",EDGE,{"derivedFrom":sQuery(id+"F40.wireOp",EDGE,"E146.MirrorCS")}),1.0]])]});
            extrude(context, id + "F41", {"entities" : qUnion([Q0, Q1, Q2, Q3]), "operationType" : NewBodyOperationType.ADD, "oppositeDirection" : true, "depth" : 30 * mm, "offsetDistance" : 25 * mm});
        }
        {
            var Q0;
            Q0=makeQuery(id+"F39.boolean.opBoolean","MERGE",FACE,{"derivedFrom":[makeQuery(id+"F37.boolean.opBoolean","COPY",FACE,{"derivedFrom":makeQuery(id+"F37.opExtrude","CAP_FACE",FACE,{"disambiguationData":[OSD([sQuery(id+"F36.wireOp",EDGE,"E130.0"),sQuery(id+"F36.wireOp",EDGE,"E132.MirrorCS"),sQuery(id+"F36.wireOp",EDGE,"E133.0"),sQuery(id+"F36.wireOp",EDGE,"E135")])],"isStart":false})})],"fromTools":[makeQuery(id+"F39.opExtrude","CAP_FACE",FACE,{"disambiguationData":[OSD([sQuery(id+"F38.wireOp",EDGE,"E136.bottom"),sQuery(id+"F38.wireOp",EDGE,"E136.top"),sQuery(id+"F38.wireOp",EDGE,"E136.left"),sQuery(id+"F38.wireOp",EDGE,"E136.right")])],"isStart":false})]});
            var sketch = newSketch(context, id + "F42", { "sketchPlane" : qUnion([Q0])});
            skLineSegment(sketch, "E149.bottom", {"start": v(-3228.16, 4478.7) * mm, "end": v(-2428.16, 4478.7) * mm});
            skLineSegment(sketch, "E149.top", {"start": v(-3228.16, 6478.7) * mm, "end": v(-2428.16, 6478.7) * mm});
            skLineSegment(sketch, "E149.left", {"start": v(-3228.16, 4478.7) * mm, "end": v(-3228.16, 6478.7) * mm});
            skLineSegment(sketch, "E149.right", {"start": v(-2428.16, 4478.7) * mm, "end": v(-2428.16, 6478.7) * mm});
            skLineSegment(sketch, "E150.0", {"start": v(-2423.16, 4478.7) * mm, "end": v(-2423.16, 6478.7) * mm});
            skLineSegment(sketch, "E151.MirrorCS", {"start": v(-2418.16, 4478.7) * mm, "end": v(-2418.16, 6478.7) * mm});
            skLineSegment(sketch, "E152.MirrorCS", {"start": v(-1618.16, 4478.7) * mm, "end": v(-2418.16, 4478.7) * mm});
            skLineSegment(sketch, "E153.MirrorCS", {"start": v(-1618.16, 4478.7) * mm, "end": v(-1618.16, 6478.7) * mm});
            skLineSegment(sketch, "E154.MirrorCS", {"start": v(-1618.16, 6478.7) * mm, "end": v(-2418.16, 6478.7) * mm});
            skSolve(sketch);
        }
        {
            var Q0;
            Q0=makeQuery(id+"F42.imprint","IMPRINT",FACE,{"disambiguationData":[TD([[makeQuery(id+"F42.imprint","IMPRINT",EDGE,{"derivedFrom":sQuery(id+"F42.wireOp",EDGE,"E151.MirrorCS")}),-1.0]])]});
            var Q1;
            Q1=makeQuery(id+"F42.imprint","IMPRINT",FACE,{"disambiguationData":[TD([[makeQuery(id+"F42.imprint","IMPRINT",EDGE,{"derivedFrom":sQuery(id+"F42.wireOp",EDGE,"E149.bottom")}),1.0]])]});
            extrude(context, id + "F43", {"entities" : qUnion([Q0, Q1]), "depth" : 120 * mm, "offsetDistance" : 25 * mm});
        }
        {
            var Q0;
            {var subQ0=sQuery(id+"F40.wireOp",EDGE,"E137.bottom");Q0=makeQuery(id+"F41.boolean.opBoolean","MERGE",FACE,{"derivedFrom":[makeQuery(id+"F7.opExtrude","SWEPT_FACE",FACE,{"disambiguationData":[OSD([sQuery(id+"F6.wireOp",EDGE,"E44")])]}),makeQuery(id+"F41.opExtrude","CAP_FACE",FACE,{"disambiguationData":[OSD([subQ0,sQuery(id+"F40.wireOp",EDGE,"E142"),sQuery(id+"F40.wireOp",EDGE,"E143"),sQuery(id+"F40.wireOp",EDGE,"E148.left")])],"isStart":true}),makeQuery(id+"F41.opExtrude","CAP_FACE",FACE,{"disambiguationData":[OSD([subQ0,sQuery(id+"F40.wireOp",EDGE,"E145.MirrorCS"),sQuery(id+"F40.wireOp",EDGE,"E146.MirrorCS"),sQuery(id+"F40.wireOp",EDGE,"E147.right")])],"isStart":true})]});}
            var sketch = newSketch(context, id + "F44", { "sketchPlane" : qUnion([Q0])});
            skLineSegment(sketch, "E155", {"start": v(4423.7, 455) * mm, "end": v(4423.7, 380) * mm, "construction": true});
            skLineSegment(sketch, "E156", {"start": v(4423.7, 380) * mm, "end": v(6533.7, 380) * mm, "construction": true});
            skLineSegment(sketch, "E157.bottom", {"start": v(6533.7, 0) * mm, "end": v(4423.7, 0) * mm});
            skLineSegment(sketch, "E157.top", {"start": v(6533.7, 380) * mm, "end": v(4423.7, 380) * mm});
            skLineSegment(sketch, "E157.left", {"start": v(6533.7, 0) * mm, "end": v(6533.7, 380) * mm});
            skLineSegment(sketch, "E157.right", {"start": v(4423.7, 0) * mm, "end": v(4423.7, 380) * mm});
            skLineSegment(sketch, "E158", {"start": v(5478.7, 0) * mm, "end": v(5478.7, 380) * mm, "construction": true});
            skLineSegment(sketch, "E159", {"start": v(4423.7, 190) * mm, "end": v(6533.7, 190) * mm, "construction": true});
            skLineSegment(sketch, "E160.bottom", {"start": v(5203.7, 315) * mm, "end": v(5753.7, 315) * mm});
            skLineSegment(sketch, "E160.top", {"start": v(5203.7, 65) * mm, "end": v(5753.7, 65) * mm});
            skLineSegment(sketch, "E160.left", {"start": v(5203.7, 315) * mm, "end": v(5203.7, 65) * mm});
            skLineSegment(sketch, "E160.right", {"start": v(5753.7, 315) * mm, "end": v(5753.7, 65) * mm});
            skLineSegment(sketch, "E161.bottom", {"start": v(4538.7, 315) * mm, "end": v(5088.7, 315) * mm});
            skLineSegment(sketch, "E161.top", {"start": v(4538.7, 65) * mm, "end": v(5088.7, 65) * mm});
            skLineSegment(sketch, "E161.left", {"start": v(4538.7, 315) * mm, "end": v(4538.7, 65) * mm});
            skLineSegment(sketch, "E161.right", {"start": v(5088.7, 315) * mm, "end": v(5088.7, 65) * mm});
            skLineSegment(sketch, "E162.bottom", {"start": v(5868.7, 315) * mm, "end": v(6418.7, 315) * mm});
            skLineSegment(sketch, "E162.top", {"start": v(5868.7, 65) * mm, "end": v(6418.7, 65) * mm});
            skLineSegment(sketch, "E162.left", {"start": v(5868.7, 315) * mm, "end": v(5868.7, 65) * mm});
            skLineSegment(sketch, "E162.right", {"start": v(6418.7, 315) * mm, "end": v(6418.7, 65) * mm});
            skSolve(sketch);
        }
        {
            var Q0;
            Q0=makeQuery(id+"F7.opExtrude","CAP_FACE",FACE,{"disambiguationData":[OSD([sQuery(id+"F6.wireOp",EDGE,"E42"),sQuery(id+"F6.wireOp",EDGE,"E43"),sQuery(id+"F6.wireOp",EDGE,"E44"),sQuery(id+"F6.wireOp",EDGE,"E45")])],"isStart":false});
            var sketch = newSketch(context, id + "F45", { "sketchPlane" : qUnion([Q0])});
            skLineSegment(sketch, "E163.bottom", {"start": v(-3268.16, 6533.7) * mm, "end": v(-3228.16, 6533.7) * mm});
            skLineSegment(sketch, "E163.top", {"start": v(-3268.16, 4423.7) * mm, "end": v(-3228.16, 4423.7) * mm});
            skLineSegment(sketch, "E163.left", {"start": v(-3268.16, 6533.7) * mm, "end": v(-3268.16, 4423.7) * mm});
            skLineSegment(sketch, "E163.right", {"start": v(-3228.16, 6533.7) * mm, "end": v(-3228.16, 4423.7) * mm});
            skSolve(sketch);
        }
        {
            var Q0;
            {var subQ2=sQuery(id+"F45.wireOp",EDGE,"E163.bottom");Q0=makeQuery(id+"F45.imprint","IMPRINT",FACE,{"disambiguationData":[TD([[makeQuery(id+"F45.imprint","IMPRINT",EDGE,{"derivedFrom":subQ2}),1.0]])]});}
            extrude(context, id + "F46", {"entities" : qUnion([Q0]), "operationType" : NewBodyOperationType.ADD, "depth" : 200 * mm, "offsetDistance" : 25 * mm});
        }
        {
            var Q0;
            Q0=makeQuery(id+"F44.imprint","IMPRINT",FACE,{"disambiguationData":[TD([[makeQuery(id+"F44.imprint","IMPRINT",EDGE,{"derivedFrom":sQuery(id+"F44.wireOp",EDGE,"E162.bottom")}),-1.0]])]});
            var Q1;
            Q1=makeQuery(id+"F44.imprint","IMPRINT",FACE,{"disambiguationData":[TD([[makeQuery(id+"F44.imprint","IMPRINT",EDGE,{"derivedFrom":sQuery(id+"F44.wireOp",EDGE,"E160.bottom")}),-1.0]])]});
            var Q2;
            Q2=makeQuery(id+"F44.imprint","IMPRINT",FACE,{"disambiguationData":[TD([[makeQuery(id+"F44.imprint","IMPRINT",EDGE,{"derivedFrom":sQuery(id+"F44.wireOp",EDGE,"E161.bottom")}),-1.0]])]});
            extrude(context, id + "F47", {"entities" : qUnion([Q0, Q1, Q2]), "depth" : 20 * mm, "offsetDistance" : 25 * mm});
        }
        {
            var Q0;
            Q0=makeQuery(id+"F47.opExtrude","CAP_FACE",FACE,{"disambiguationData":[OSD([sQuery(id+"F44.wireOp",EDGE,"E162.bottom"),sQuery(id+"F44.wireOp",EDGE,"E162.top"),sQuery(id+"F44.wireOp",EDGE,"E162.left"),sQuery(id+"F44.wireOp",EDGE,"E162.right")])],"isStart":false});
            var sketch = newSketch(context, id + "F48", { "sketchPlane" : qUnion([Q0])});
            skLineSegment(sketch, "E164", {"start": v(4813.7, 315) * mm, "end": v(4813.7, 65) * mm, "construction": true});
            skCircle(sketch, "E165", {"center": v(4813.7, 190) * mm, "radius": 15 * mm});
            skLineSegment(sketch, "E166", {"start": v(5478.7, 315) * mm, "end": v(5478.7, 65) * mm, "construction": true});
            skCircle(sketch, "E167", {"center": v(5478.7, 190) * mm, "radius": 15 * mm});
            skLineSegment(sketch, "E168", {"start": v(6143.7, 315) * mm, "end": v(6143.7, 65) * mm, "construction": true});
            skCircle(sketch, "E169", {"center": v(6143.7, 190) * mm, "radius": 15 * mm});
            skSolve(sketch);
        }
        {
            var Q0;
            Q0=makeQuery(id+"F48.imprint","IMPRINT",FACE,{"disambiguationData":[TD([[makeQuery(id+"F48.imprint","IMPRINT",EDGE,{"derivedFrom":sQuery(id+"F48.wireOp",EDGE,"E165")}),1.0]])]});
            var Q1;
            Q1=makeQuery(id+"F48.imprint","IMPRINT",FACE,{"disambiguationData":[TD([[makeQuery(id+"F48.imprint","IMPRINT",EDGE,{"derivedFrom":sQuery(id+"F48.wireOp",EDGE,"E167")}),1.0]])]});
            var Q2;
            Q2=makeQuery(id+"F48.imprint","IMPRINT",FACE,{"disambiguationData":[TD([[makeQuery(id+"F48.imprint","IMPRINT",EDGE,{"derivedFrom":sQuery(id+"F48.wireOp",EDGE,"E169")}),1.0]])]});
            extrude(context, id + "F49", {"entities" : qUnion([Q0, Q1, Q2]), "operationType" : NewBodyOperationType.ADD, "depth" : 10 * mm, "offsetDistance" : 25 * mm});
        }
        {
            var Q0;
            {var subQ2=sQuery(id+"F6.wireOp",EDGE,"E43");var subQ3=makeQuery(id+"F7.opExtrude","CAP_FACE",FACE,{"disambiguationData":[OSD([sQuery(id+"F6.wireOp",EDGE,"E42"),subQ2,sQuery(id+"F6.wireOp",EDGE,"E44"),sQuery(id+"F6.wireOp",EDGE,"E45")])],"isStart":false});var subQ5=makeQuery(id+"F7.opExtrude","SWEPT_FACE",FACE,{"disambiguationData":[OSD([subQ2])]});Q0=makeQuery(id+"F46.boolean.opBoolean","SPLIT",FACE,{"disambiguationData":[TD([subQ5])],"derivedFrom":subQ3});}
            var sketch = newSketch(context, id + "F50", { "sketchPlane" : qUnion([Q0])});
            skLineSegment(sketch, "E170.left", {"start": v(-3228.16, 4463.7) * mm, "end": v(-3228.16, 4423.7) * mm});
            skLineSegment(sketch, "E171.0", {"start": v(-3228.16, 4473.7) * mm, "end": v(-2368.16, 4473.7) * mm});
            skLineSegment(sketch, "E172.0", {"start": v(-2368.16, 4473.7) * mm, "end": v(-2368.16, 4413.7) * mm});
            skLineSegment(sketch, "E173.0", {"start": v(-3228.16, 4413.7) * mm, "end": v(-2368.16, 4413.7) * mm});
            skLineSegment(sketch, "E174", {"start": v(-3228.16, 4473.7) * mm, "end": v(-3228.16, 4413.7) * mm});
            skLineSegment(sketch, "E175", {"start": v(-3228.16, 5478.7) * mm, "end": v(-2438.88, 5478.7) * mm, "construction": true});
            skLineSegment(sketch, "E176.MirrorCS", {"start": v(-3228.16, 6483.7) * mm, "end": v(-2368.16, 6483.7) * mm});
            skLineSegment(sketch, "E177.MirrorCS", {"start": v(-3228.16, 6543.7) * mm, "end": v(-2368.16, 6543.7) * mm});
            skLineSegment(sketch, "E178.MirrorCS", {"start": v(-3228.16, 6483.7) * mm, "end": v(-3228.16, 6543.7) * mm});
            skLineSegment(sketch, "E179.MirrorCS", {"start": v(-2368.16, 6483.7) * mm, "end": v(-2368.16, 6543.7) * mm});
            skSolve(sketch);
        }
        {
            var Q0;
            {var subQ5=sQuery(id+"F50.wireOp",EDGE,"E171.0");Q0=makeQuery(id+"F50.imprint","IMPRINT",FACE,{"disambiguationData":[TD([[makeQuery(id+"F50.imprint","IMPRINT",EDGE,{"derivedFrom":subQ5}),-1.0]])]});}
            var Q1;
            Q1=makeQuery(id+"F50.imprint","IMPRINT",FACE,{"disambiguationData":[TD([[makeQuery(id+"F50.imprint","IMPRINT",EDGE,{"derivedFrom":sQuery(id+"F50.wireOp",EDGE,"E176.MirrorCS")}),1.0]])]});
            extrude(context, id + "F51", {"entities" : qUnion([Q0, Q1]), "operationType" : NewBodyOperationType.ADD, "oppositeDirection" : true, "depth" : 20 * mm, "offsetDistance" : 25 * mm});
        }
        {
            var Q0;
            Q0=makeQuery(id+"F46.boolean.opBoolean","MERGE",FACE,{"derivedFrom":[makeQuery(id+"F37.boolean.opBoolean","COPY",FACE,{"derivedFrom":makeQuery(id+"F37.opExtrude","SWEPT_FACE",FACE,{"disambiguationData":[OSD([sQuery(id+"F36.wireOp",EDGE,"E133.0")])]})}),makeQuery(id+"F46.opExtrude","SWEPT_FACE",FACE,{"disambiguationData":[OSD([sQuery(id+"F45.wireOp",EDGE,"E163.right")])]})]});
            var sketch = newSketch(context, id + "F52", { "sketchPlane" : qUnion([Q0])});
            skLineSegment(sketch, "E180.0", {"start": v(4433.7, 995) * mm, "end": v(4433.7, 800) * mm});
            skLineSegment(sketch, "E181.0", {"start": v(6523.7, 990) * mm, "end": v(4438.7, 990) * mm});
            skLineSegment(sketch, "E182.0", {"start": v(6523.7, 990) * mm, "end": v(6523.7, 800) * mm});
            skLineSegment(sketch, "E183.0", {"start": v(6528.7, 995) * mm, "end": v(4433.7, 995) * mm});
            skLineSegment(sketch, "E184.0", {"start": v(6528.7, 995) * mm, "end": v(6528.7, 800) * mm});
            skLineSegment(sketch, "E185.0", {"start": v(4438.7, 990) * mm, "end": v(4438.7, 800) * mm});
            skSolve(sketch);
        }
        {
            var Q0;
            {var subQ1=sQuery(id+"F52.wireOp",EDGE,"E180.0");Q0=makeQuery(id+"F52.imprint","IMPRINT",FACE,{"disambiguationData":[TD([[makeQuery(id+"F52.imprint","IMPRINT",EDGE,{"derivedFrom":subQ1}),1.0]])]});}
            extrude(context, id + "F53", {"entities" : qUnion([Q0]), "operationType" : NewBodyOperationType.REMOVE, "oppositeDirection" : true, "depth" : 5 * mm, "offsetDistance" : 25 * mm});
        }
    });
